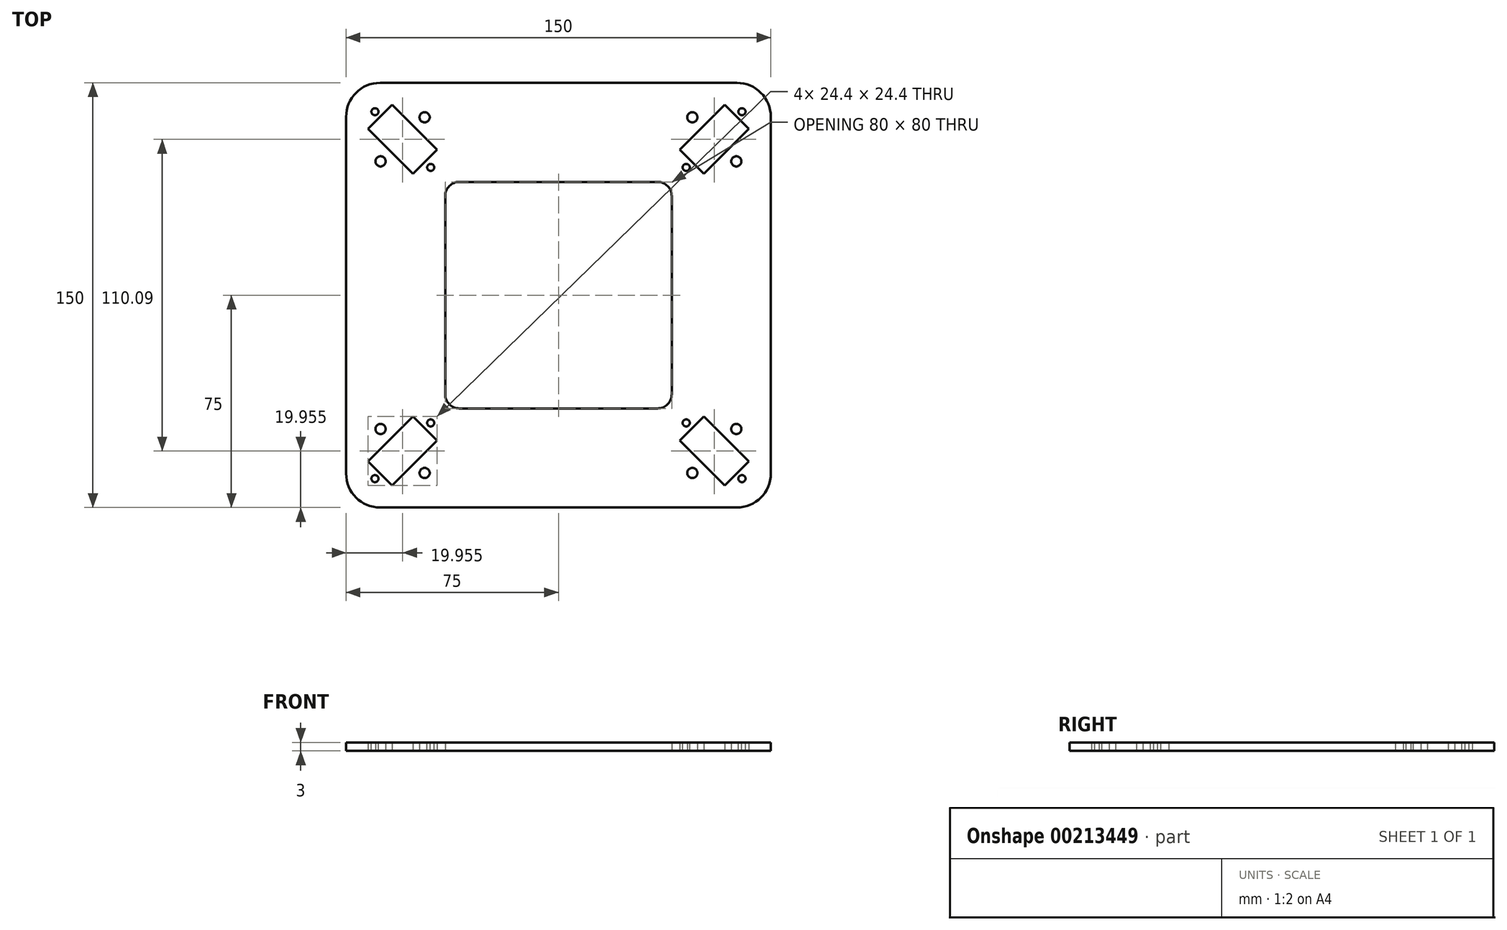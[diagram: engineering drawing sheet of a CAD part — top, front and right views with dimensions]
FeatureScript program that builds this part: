
annotation { "Feature Type Name" : "Feature", "Feature Type Description" : "" }
export const myFeature = defineFeature(function(context is Context, id is Id, definition is map)
    precondition{}
    {
        {
            var Q0;
            Q0=qCreatedBy(makeId("Top.planeOp"),FACE);
            var sketch = newSketch(context, id + "F0", { "sketchPlane" : qUnion([Q0])});
            skLineSegment(sketch, "E0.bottom", {"start": v(-63, 75) * mm, "end": v(63, 75) * mm});
            skLineSegment(sketch, "E0.top", {"start": v(-63, -75) * mm, "end": v(63, -75) * mm});
            skLineSegment(sketch, "E0.left", {"start": v(-75, 63) * mm, "end": v(-75, -63) * mm});
            skLineSegment(sketch, "E0.right", {"start": v(75, 63) * mm, "end": v(75, -63) * mm});
            skLineSegment(sketch, "E1", {"start": v(-58.76, 67.24) * mm, "end": v(-67.24, 58.76) * mm});
            skLineSegment(sketch, "E2", {"start": v(-67.24, 58.76) * mm, "end": v(-51.33, 42.85) * mm});
            skLineSegment(sketch, "E3", {"start": v(-51.33, 42.85) * mm, "end": v(-42.85, 51.33) * mm});
            skLineSegment(sketch, "E4", {"start": v(-42.85, 51.33) * mm, "end": v(-58.76, 67.24) * mm});
            skPoint(sketch, "E5.visualSharp", {"position": v(-75, 75) * mm});
            skArc(sketch, "E5.filletArc", {"start": v(-63, 75) * mm, "mid": v(-71.49, 71.49) * mm, "end": v(-75, 63) * mm});
            skLineSegment(sketch, "E6.MirrorCS", {"start": v(42.85, 51.33) * mm, "end": v(58.76, 67.24) * mm});
            skLineSegment(sketch, "E7.MirrorCS", {"start": v(67.24, 58.76) * mm, "end": v(51.33, 42.85) * mm});
            skLineSegment(sketch, "E8.MirrorCS", {"start": v(51.33, 42.85) * mm, "end": v(42.85, 51.33) * mm});
            skLineSegment(sketch, "E9.MirrorCS", {"start": v(58.76, 67.24) * mm, "end": v(67.24, 58.76) * mm});
            skLineSegment(sketch, "E10.MirrorCS", {"start": v(51.33, -42.85) * mm, "end": v(42.85, -51.33) * mm});
            skLineSegment(sketch, "E11.MirrorCS", {"start": v(-67.24, -58.76) * mm, "end": v(-51.33, -42.85) * mm});
            skLineSegment(sketch, "E12.MirrorCS", {"start": v(-51.33, -42.85) * mm, "end": v(-42.85, -51.33) * mm});
            skLineSegment(sketch, "E13.MirrorCS", {"start": v(-42.85, -51.33) * mm, "end": v(-58.76, -67.24) * mm});
            skLineSegment(sketch, "E14.MirrorCS", {"start": v(-58.76, -67.24) * mm, "end": v(-67.24, -58.76) * mm});
            skLineSegment(sketch, "E15.MirrorCS", {"start": v(67.24, -58.76) * mm, "end": v(51.33, -42.85) * mm});
            skLineSegment(sketch, "E16.MirrorCS", {"start": v(42.85, -51.33) * mm, "end": v(58.76, -67.24) * mm});
            skLineSegment(sketch, "E17.MirrorCS", {"start": v(58.76, -67.24) * mm, "end": v(67.24, -58.76) * mm});
            skPoint(sketch, "E18.visualSharp", {"position": v(75, 75) * mm});
            skArc(sketch, "E18.filletArc", {"start": v(75, 63) * mm, "mid": v(71.49, 71.49) * mm, "end": v(63, 75) * mm});
            skPoint(sketch, "E19.visualSharp", {"position": v(75, -75) * mm});
            skArc(sketch, "E19.filletArc", {"start": v(63, -75) * mm, "mid": v(71.49, -71.49) * mm, "end": v(75, -63) * mm});
            skPoint(sketch, "E20.visualSharp", {"position": v(-75, -75) * mm});
            skArc(sketch, "E20.filletArc", {"start": v(-75, -63) * mm, "mid": v(-71.49, -71.49) * mm, "end": v(-63, -75) * mm});
            skLineSegment(sketch, "E21.bottom", {"start": v(0, 0) * mm, "end": v(-40, 0) * mm});
            skLineSegment(sketch, "E21.top", {"start": v(0, 40) * mm, "end": v(-35, 40) * mm});
            skLineSegment(sketch, "E21.left", {"start": v(0, 0) * mm, "end": v(0, 40) * mm});
            skLineSegment(sketch, "E21.right", {"start": v(-40, 0) * mm, "end": v(-40, 35) * mm});
            skLineSegment(sketch, "E22.MirrorCS", {"start": v(0, 0) * mm, "end": v(0, -40) * mm});
            skLineSegment(sketch, "E23.MirrorCS", {"start": v(0, -40) * mm, "end": v(-35, -40) * mm});
            skLineSegment(sketch, "E24.MirrorCS", {"start": v(-40, 0) * mm, "end": v(-40, -35) * mm});
            skLineSegment(sketch, "E25.MirrorCS", {"start": v(0, 40) * mm, "end": v(35, 40) * mm});
            skLineSegment(sketch, "E26.MirrorCS", {"start": v(40, 0) * mm, "end": v(40, 35) * mm});
            skLineSegment(sketch, "E27.MirrorCS", {"start": v(40, 0) * mm, "end": v(40, -35) * mm});
            skLineSegment(sketch, "E28.MirrorCS", {"start": v(0, -40) * mm, "end": v(35, -40) * mm});
            skPoint(sketch, "E29.visualSharp", {"position": v(-40, 40) * mm});
            skArc(sketch, "E29.filletArc", {"start": v(-35, 40) * mm, "mid": v(-38.54, 38.54) * mm, "end": v(-40, 35) * mm});
            skPoint(sketch, "E30.visualSharp", {"position": v(40, 40) * mm});
            skArc(sketch, "E30.filletArc", {"start": v(40, 35) * mm, "mid": v(38.54, 38.54) * mm, "end": v(35, 40) * mm});
            skPoint(sketch, "E31.visualSharp", {"position": v(40, -40) * mm});
            skArc(sketch, "E31.filletArc", {"start": v(35, -40) * mm, "mid": v(38.54, -38.54) * mm, "end": v(40, -35) * mm});
            skPoint(sketch, "E32.visualSharp", {"position": v(-40, -40) * mm});
            skArc(sketch, "E32.filletArc", {"start": v(-40, -35) * mm, "mid": v(-38.54, -38.54) * mm, "end": v(-35, -40) * mm});
            skLineSegment(sketch, "E33", {"start": v(-50.8, 59.29) * mm, "end": v(-62.82, 47.27) * mm, "construction": true});
            skLineSegment(sketch, "E34", {"start": v(-50.8, 59.29) * mm, "end": v(-47.27, 62.82) * mm, "construction": true});
            skCircle(sketch, "E35", {"center": v(-47.27, 62.82) * mm, "radius": 1.8 * mm});
            skCircle(sketch, "E36", {"center": v(-62.82, 47.27) * mm, "radius": 1.8 * mm});
            skCircle(sketch, "E37.MirrorC", {"center": v(62.82, 47.27) * mm, "radius": 1.8 * mm});
            skCircle(sketch, "E38.MirrorC", {"center": v(47.27, 62.82) * mm, "radius": 1.8 * mm});
            skCircle(sketch, "E39.MirrorC", {"center": v(62.82, -47.27) * mm, "radius": 1.8 * mm});
            skCircle(sketch, "E40.MirrorC", {"center": v(47.27, -62.82) * mm, "radius": 1.8 * mm});
            skCircle(sketch, "E41.MirrorC", {"center": v(-47.27, -62.82) * mm, "radius": 1.8 * mm});
            skCircle(sketch, "E42.MirrorC", {"center": v(-62.82, -47.27) * mm, "radius": 1.8 * mm});
            skSolve(sketch);
        }
        {
            var Q0;
            Q0=makeQuery(id+"F0.imprint","IMPRINT",FACE,{"disambiguationData":[TD([[makeQuery(id+"F0.imprint","IMPRINT",EDGE,{"derivedFrom":sQuery(id+"F0.wireOp",EDGE,"E0.bottom")}),-1.0]])]});
            extrude(context, id + "F1", {"entities" : qUnion([Q0]), "depth" : 3 * mm});
        }
        {
            var Q0;
            Q0=makeQuery(id+"F1.opExtrude","CAP_FACE",FACE,{"disambiguationData":[OSD([sQuery(id+"F0.wireOp",EDGE,"E0.bottom"),sQuery(id+"F0.wireOp",EDGE,"E0.top"),sQuery(id+"F0.wireOp",EDGE,"E0.left"),sQuery(id+"F0.wireOp",EDGE,"E0.right"),sQuery(id+"F0.wireOp",EDGE,"E1"),sQuery(id+"F0.wireOp",EDGE,"E2"),sQuery(id+"F0.wireOp",EDGE,"E3"),sQuery(id+"F0.wireOp",EDGE,"E4"),sQuery(id+"F0.wireOp",EDGE,"E5.filletArc"),sQuery(id+"F0.wireOp",EDGE,"E6.MirrorCS"),sQuery(id+"F0.wireOp",EDGE,"E7.MirrorCS"),sQuery(id+"F0.wireOp",EDGE,"E8.MirrorCS"),sQuery(id+"F0.wireOp",EDGE,"E9.MirrorCS"),sQuery(id+"F0.wireOp",EDGE,"E10.MirrorCS"),sQuery(id+"F0.wireOp",EDGE,"E11.MirrorCS"),sQuery(id+"F0.wireOp",EDGE,"E12.MirrorCS"),sQuery(id+"F0.wireOp",EDGE,"E13.MirrorCS"),sQuery(id+"F0.wireOp",EDGE,"E14.MirrorCS"),sQuery(id+"F0.wireOp",EDGE,"E15.MirrorCS"),sQuery(id+"F0.wireOp",EDGE,"E16.MirrorCS"),sQuery(id+"F0.wireOp",EDGE,"E17.MirrorCS"),sQuery(id+"F0.wireOp",EDGE,"E18.filletArc"),sQuery(id+"F0.wireOp",EDGE,"E19.filletArc"),sQuery(id+"F0.wireOp",EDGE,"E20.filletArc"),sQuery(id+"F0.wireOp",EDGE,"E21.top"),sQuery(id+"F0.wireOp",EDGE,"E21.right"),sQuery(id+"F0.wireOp",EDGE,"E23.MirrorCS"),sQuery(id+"F0.wireOp",EDGE,"E24.MirrorCS"),sQuery(id+"F0.wireOp",EDGE,"E25.MirrorCS"),sQuery(id+"F0.wireOp",EDGE,"E26.MirrorCS"),sQuery(id+"F0.wireOp",EDGE,"E27.MirrorCS"),sQuery(id+"F0.wireOp",EDGE,"E28.MirrorCS")])],"isStart":false});
            var sketch = newSketch(context, id + "F2", { "sketchPlane" : qUnion([Q0])});
            skCircle(sketch, "E43", {"center": v(-64.8, -64.8) * mm, "radius": 1.25 * mm});
            skCircle(sketch, "E44", {"center": v(-45.12, -45.12) * mm, "radius": 1.25 * mm});
            skCircle(sketch, "E45.1.0", {"center": v(45.12, -45.12) * mm, "radius": 1.25 * mm});
            skCircle(sketch, "E45.2.0", {"center": v(45.12, 45.12) * mm, "radius": 1.25 * mm});
            skCircle(sketch, "E45.3.0", {"center": v(-45.12, 45.12) * mm, "radius": 1.25 * mm});
            skPoint(sketch, "E45.center", {"position": v(0, 0) * mm});
            skCircle(sketch, "E46.1.0", {"center": v(64.8, -64.8) * mm, "radius": 1.25 * mm});
            skCircle(sketch, "E46.2.0", {"center": v(64.8, 64.8) * mm, "radius": 1.25 * mm});
            skCircle(sketch, "E46.3.0", {"center": v(-64.8, 64.8) * mm, "radius": 1.25 * mm});
            skSolve(sketch);
        }
        {
            var Q0;
            Q0 = qSketchRegion(id + "F2", true);
            extrude(context, id + "F3", {"entities" : qUnion([Q0]), "operationType" : NewBodyOperationType.REMOVE, "endBound" : BoundingType.THROUGH_ALL, "oppositeDirection" : true, "depth" : 25 * mm});
        }
        {
            var Q0;
            Q0=makeQuery(id+"F1.opExtrude","SWEPT_BODY",BODY,{"disambiguationData":[OSD([sQuery(id+"F0.wireOp",EDGE,"E0.bottom"),sQuery(id+"F0.wireOp",EDGE,"E0.top"),sQuery(id+"F0.wireOp",EDGE,"E0.left"),sQuery(id+"F0.wireOp",EDGE,"E0.right"),sQuery(id+"F0.wireOp",EDGE,"E1"),sQuery(id+"F0.wireOp",EDGE,"E2"),sQuery(id+"F0.wireOp",EDGE,"E3"),sQuery(id+"F0.wireOp",EDGE,"E4"),sQuery(id+"F0.wireOp",EDGE,"E5.filletArc"),sQuery(id+"F0.wireOp",EDGE,"E6.MirrorCS"),sQuery(id+"F0.wireOp",EDGE,"E7.MirrorCS"),sQuery(id+"F0.wireOp",EDGE,"E8.MirrorCS"),sQuery(id+"F0.wireOp",EDGE,"E9.MirrorCS"),sQuery(id+"F0.wireOp",EDGE,"E10.MirrorCS"),sQuery(id+"F0.wireOp",EDGE,"E11.MirrorCS"),sQuery(id+"F0.wireOp",EDGE,"E12.MirrorCS"),sQuery(id+"F0.wireOp",EDGE,"E13.MirrorCS"),sQuery(id+"F0.wireOp",EDGE,"E14.MirrorCS"),sQuery(id+"F0.wireOp",EDGE,"E15.MirrorCS"),sQuery(id+"F0.wireOp",EDGE,"E16.MirrorCS"),sQuery(id+"F0.wireOp",EDGE,"E17.MirrorCS"),sQuery(id+"F0.wireOp",EDGE,"E18.filletArc"),sQuery(id+"F0.wireOp",EDGE,"E19.filletArc"),sQuery(id+"F0.wireOp",EDGE,"E20.filletArc"),sQuery(id+"F0.wireOp",EDGE,"E21.top"),sQuery(id+"F0.wireOp",EDGE,"E21.right"),sQuery(id+"F0.wireOp",EDGE,"E23.MirrorCS"),sQuery(id+"F0.wireOp",EDGE,"E24.MirrorCS"),sQuery(id+"F0.wireOp",EDGE,"E25.MirrorCS"),sQuery(id+"F0.wireOp",EDGE,"E26.MirrorCS"),sQuery(id+"F0.wireOp",EDGE,"E27.MirrorCS"),sQuery(id+"F0.wireOp",EDGE,"E28.MirrorCS"),sQuery(id+"F0.wireOp",EDGE,"E29.filletArc"),sQuery(id+"F0.wireOp",EDGE,"E30.filletArc"),sQuery(id+"F0.wireOp",EDGE,"E31.filletArc"),sQuery(id+"F0.wireOp",EDGE,"E32.filletArc")])]});
            transform(context, id + "F4", {"entities" : qUnion([Q0]), "transformType" : TransformType.TRANSLATION_3D, "dx" : 0 * mm, "dy" : 0 * mm, "dz" : 20 * mm, "makeCopy" : true});
        }
        {
            var Q0;
            Q0=makeQuery(id+"F4.opPattern","COPY",BODY,{"derivedFrom":makeQuery(id+"F1.opExtrude","SWEPT_BODY",BODY,{"disambiguationData":[OSD([sQuery(id+"F0.wireOp",EDGE,"E0.bottom"),sQuery(id+"F0.wireOp",EDGE,"E0.top"),sQuery(id+"F0.wireOp",EDGE,"E0.left"),sQuery(id+"F0.wireOp",EDGE,"E0.right"),sQuery(id+"F0.wireOp",EDGE,"E1"),sQuery(id+"F0.wireOp",EDGE,"E2"),sQuery(id+"F0.wireOp",EDGE,"E3"),sQuery(id+"F0.wireOp",EDGE,"E4"),sQuery(id+"F0.wireOp",EDGE,"E5.filletArc"),sQuery(id+"F0.wireOp",EDGE,"E6.MirrorCS"),sQuery(id+"F0.wireOp",EDGE,"E7.MirrorCS"),sQuery(id+"F0.wireOp",EDGE,"E8.MirrorCS"),sQuery(id+"F0.wireOp",EDGE,"E9.MirrorCS"),sQuery(id+"F0.wireOp",EDGE,"E10.MirrorCS"),sQuery(id+"F0.wireOp",EDGE,"E11.MirrorCS"),sQuery(id+"F0.wireOp",EDGE,"E12.MirrorCS"),sQuery(id+"F0.wireOp",EDGE,"E13.MirrorCS"),sQuery(id+"F0.wireOp",EDGE,"E14.MirrorCS"),sQuery(id+"F0.wireOp",EDGE,"E15.MirrorCS"),sQuery(id+"F0.wireOp",EDGE,"E16.MirrorCS"),sQuery(id+"F0.wireOp",EDGE,"E17.MirrorCS"),sQuery(id+"F0.wireOp",EDGE,"E18.filletArc"),sQuery(id+"F0.wireOp",EDGE,"E19.filletArc"),sQuery(id+"F0.wireOp",EDGE,"E20.filletArc"),sQuery(id+"F0.wireOp",EDGE,"E21.top"),sQuery(id+"F0.wireOp",EDGE,"E21.right"),sQuery(id+"F0.wireOp",EDGE,"E23.MirrorCS"),sQuery(id+"F0.wireOp",EDGE,"E24.MirrorCS"),sQuery(id+"F0.wireOp",EDGE,"E25.MirrorCS"),sQuery(id+"F0.wireOp",EDGE,"E26.MirrorCS"),sQuery(id+"F0.wireOp",EDGE,"E27.MirrorCS"),sQuery(id+"F0.wireOp",EDGE,"E28.MirrorCS"),sQuery(id+"F0.wireOp",EDGE,"E29.filletArc"),sQuery(id+"F0.wireOp",EDGE,"E30.filletArc"),sQuery(id+"F0.wireOp",EDGE,"E31.filletArc"),sQuery(id+"F0.wireOp",EDGE,"E32.filletArc")])]}),"instanceName":"1"});
            deleteBodies(context, id + "F5", {"entities" : qUnion([Q0])});
        }
    });
